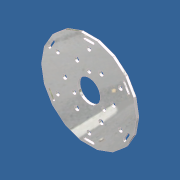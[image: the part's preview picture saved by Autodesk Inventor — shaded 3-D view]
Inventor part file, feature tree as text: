
AUTODESK INVENTOR PART (.ipt)
format: ipt  version: unknown  size: 262,656 bytes
history: native  units: in
note: dims shown in document units (in); Inventor stores cm internally (conversion verified against a paired STEP export)
features: extrude x1, sketch x1
ambient origin geometry x8: Origin, YZ Plane, XZ Plane, XY Plane, X Axis, Y Axis, Z Axis, Center Point
bodies: Solid1 (feature_tree)
feature tree (2):
  extrude  "Extrusion1"  Depth=0.1705in
  sketch  "Sketch1"  dims[d1=0.095in d2=0.335in d7=0.1705in d9=0.192in d11=0.221in d13=0.6625in d14=0.875in d16=1.687in d17=2.3622in d19=360.0deg d23=1.1811in d25=360.0deg d27=2.3622in d29=360.0deg d31=0.095in d32=0.0in d33=3.625in d35=0.335in d36=3.25in]
